# Revit family: Grohe_PlumbingFixtures_SingleLeverSinkMixer_30590KF0
name_source: partatom
category: Plumbing Fixtures
units: mm (PartAtom-declared; Revit-internal decimal feet)

## family parameters
Cut with Voids When Loaded = No
Host = Face
OmniClass Number = 23.65.05.11.11
OmniClass Title = Water Supply Systems
Part Type = Normal
Room Calculation Point = No
Round Connector Dimension = Use Diameter
Shared = No

## types (1)
- 30590KF0
    Assembly Code = D2020
    AssetType = Fixed
    BIMObjectName = Grohe_PlumbingFixtures_SingleLeverSinkMixer_30590KF0
    CO2NeutralProduction = GROHE is one of the first leading manufacturer within the sanitary industry having a CO2-neutral production.
    CW Connection = Yes
    ClassificationName = Uniclass2015
    ClassificationValue = Ss_55_70_38_45
    Color = Black
    Cost = 0 $
    Default Elevation = 0 mm  [stored 0 ft]
    Description = Consisting of:
GROHE Blue single-lever sink mixer with filter function
monobloc installation
L-spout
pull out mousseur spout
separate handle for filtered water
28 mm ceramic cartridge with GROHE SilkMove
swivel tubular spout
swivel area 360°
separate inner water ways for filtered and non-filtered water
flexible connection hoses
    DocumentationCertificates = https://www.bimstore.co
    DocumentationInstallationGuide = https://www.bimstore.co
    DocumentationLiterature = https://www.bimstore.co
    DocumentationMaintenance = https://www.bimstore.co
    DocumentationTechnical = https://www.bimstore.co
    DurationUnit = Year
    EF000003 = Top/tap hole
    EF000139 = Lacquered
    EF000329 = true
    EF002286 = Hose (gland nut)
    EF002671 = Black
    EF003625 = 0
    EF020779 = true
    EF020785 = 3/8 inch
    EF020791 = Brass
    EF020795 = Rotating, top
    EF020871 = true
    EF020872 = true
    EF020873 = false
    EF021808 = 1-hole
    EF022042 = Z
    EF022750 = Pipe
    EF023061 = 1.0 Pa
    EF023688 = Foam jet nozzle
    EF023957 = FALSE
    EF025109 = Other
    EFDE0022 = None
    Ecojoy = No
    ExpectedLife = 0
    FullRecyclabilityOfPlastic = All plastic components are fully recycable
    GROHESocialCommittment = green.grohe.com/social_engagement
    GROHESustainability = green.grohe.com
    HW Connection = Yes
    IfcExportAs = IfcPipeFitting
    IfcExportType = IfcPipeFittingType
    Keynote = N13
    Manufacturer = Grohe
    ManufacturerName = Grohe
    Material = Other
    Model = 30590KF0
    ModelNumber = 30590KF0
    ModelReference = Faucet and M size boiler
    NBSDescription = Hot and cold water supply systems
    NBSObjectName = Grohe - Hot and cold water supply systems
    NBSReference = 55-40-40/140
    NominalDepth = 0 mm  [stored 0 ft]
    NominalHeight = 0 mm  [stored 0 ft]
    NominalLength = 0 mm  [stored 0 ft]
    PrimaryMaterial = GROHE - Black
    ProductDescription = Consisting of:
GROHE Blue single-lever sink mixer with filter function
monobloc installation
L-spout
pull out mousseur spout
separate handle for filtered water
28 mm ceramic cartridge with GROHE SilkMove
swivel tubular spout
swivel area 360°
separate inner water ways for filtered and non-filtered water
flexible connection hoses
    ProductNumber = 30590KF0
    ProductShortText = Faucet and M size boiler
    ProductType = Single Lever Mixer
    ProductionYear = 2022
    SustainabilityAward = green.grohe.com/awards
    SustainabilityReport = green.grohe.com/reporting
    TPIDocumentLink = https://cdn.cloud.grohe.com
    Type Comments = Faucet and M size boiler
    TypeName = Faucet and M size boiler
    URL = https://www.grohe.co.uk
    Vent Connection = No
    WarrantyDurationLabor = 0
    WarrantyDurationParts = 0
    WarrantyDurationUnit = Year
    Waste Connection = No
    _BSBibleVersion = 16
    _BimSpecGuid = 0
    _CurrentRevision = 1
    _DistributedBy = https://www.bimstore.co
    _ObjectUserGuide = https://www.bimstore.co

note: [stored X ft] marks values corroborated as IEEE doubles in the binary element streams (Revit-internal decimal feet)

## geometry (parser evidence)
native form markers: Sweep x1
no freeform markers — native parametric forms only
